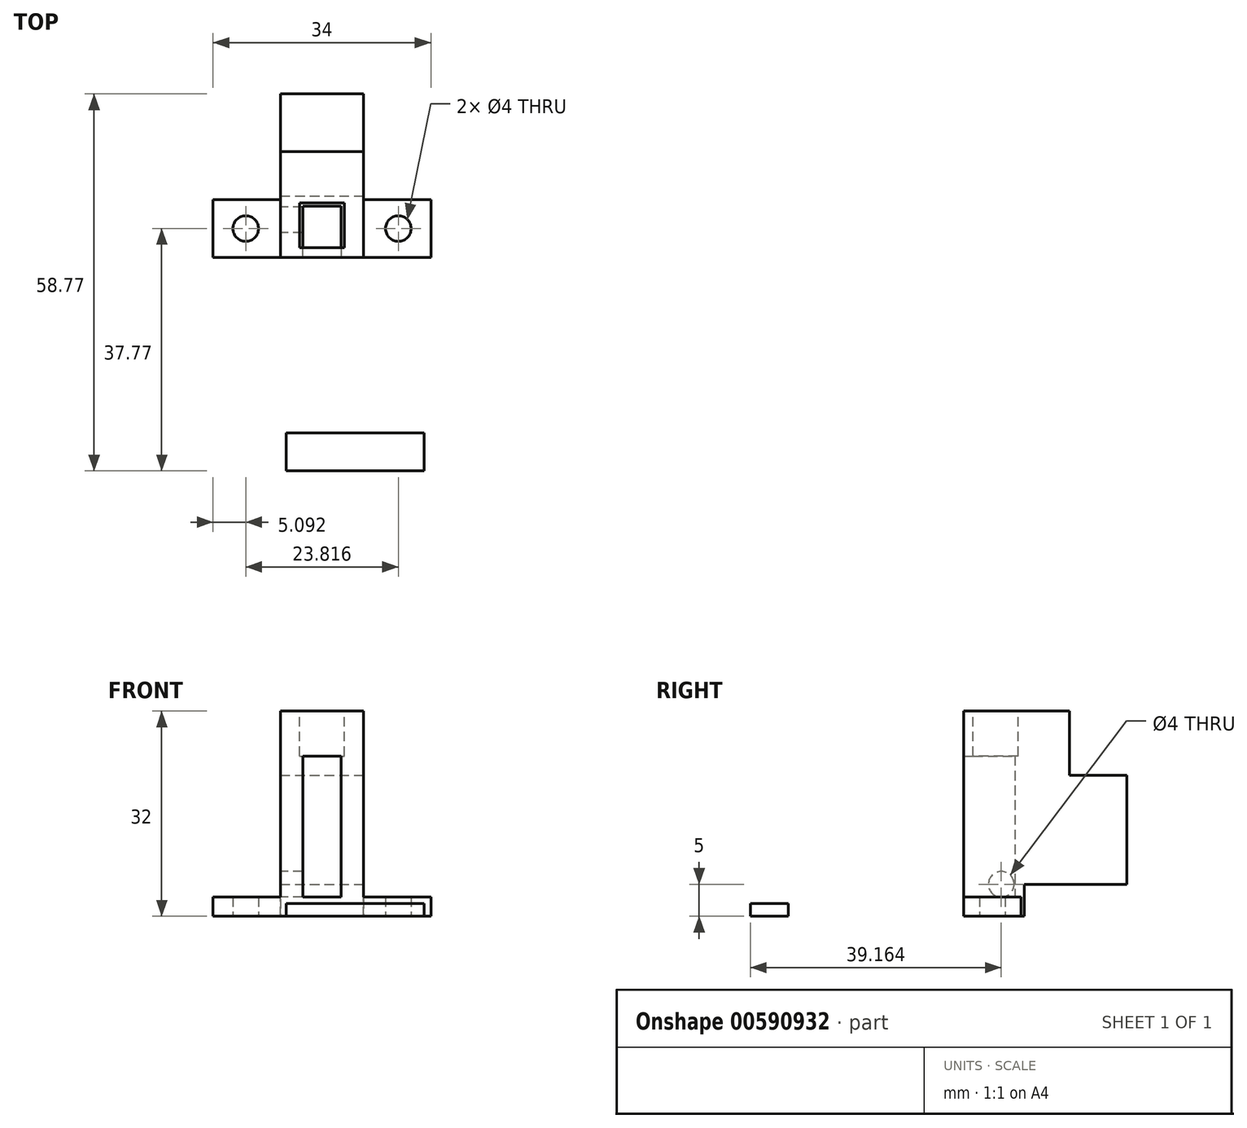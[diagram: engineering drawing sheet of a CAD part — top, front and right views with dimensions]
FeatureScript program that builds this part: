
annotation { "Feature Type Name" : "Feature", "Feature Type Description" : "" }
export const myFeature = defineFeature(function(context is Context, id is Id, definition is map)
    precondition{}
    {
        {
            var Q0;
            Q0=qCreatedBy(makeId("Top.planeOp"),FACE);
            var sketch = newSketch(context, id + "F0", { "sketchPlane" : qUnion([Q0])});
            skLineSegment(sketch, "E0.bottom", {"start": v(-6.5, 20.5) * mm, "end": v(6.5, 20.5) * mm});
            skLineSegment(sketch, "E0.top", {"start": v(-6.5, -5) * mm, "end": v(6.5, -5) * mm});
            skLineSegment(sketch, "E0.left", {"start": v(-6.5, 20.5) * mm, "end": v(-6.5, -5) * mm});
            skLineSegment(sketch, "E0.right", {"start": v(6.5, 20.5) * mm, "end": v(6.5, -5) * mm});
            skSolve(sketch);
        }
        {
            var Q0;
            Q0=makeQuery(id+"F0.imprint","IMPRINT",FACE,{"disambiguationData":[TD([[makeQuery(id+"F0.imprint","IMPRINT",EDGE,{"derivedFrom":sQuery(id+"F0.wireOp",EDGE,"E0.bottom")}),-1.0]])]});
            var Q1;
            Q1=makeQuery(id+"F0.imprint","IMPRINT",FACE,{"disambiguationData":[TD([[makeQuery(id+"F0.imprint","IMPRINT",EDGE,{"derivedFrom":sQuery(id+"F0.wireOp",EDGE,"DMgWt05r-v9AS-qHSY-Eq6J-6PHM9xyc8q6q.bottom")}),-1.0]])]});
            extrude(context, id + "F1", {"entities" : qUnion([Q0, Q1]), "depth" : 32 * mm, "offsetDistance" : 25 * mm});
        }
        {
            var Q0;
            Q0=makeQuery(id+"F1.opExtrude","CAP_FACE",FACE,{"disambiguationData":[OSD([sQuery(id+"F0.wireOp",EDGE,"E0.bottom"),sQuery(id+"F0.wireOp",EDGE,"E0.top"),sQuery(id+"F0.wireOp",EDGE,"E0.left"),sQuery(id+"F0.wireOp",EDGE,"E0.right")])],"isStart":false});
            var sketch = newSketch(context, id + "F2", { "sketchPlane" : qUnion([Q0])});
            skLineSegment(sketch, "E1.bottom", {"start": v(-3.5, 3.5) * mm, "end": v(3.5, 3.5) * mm});
            skLineSegment(sketch, "E1.top", {"start": v(-3.5, -3.5) * mm, "end": v(3.5, -3.5) * mm});
            skLineSegment(sketch, "E1.left", {"start": v(-3.5, 3.5) * mm, "end": v(-3.5, -3.5) * mm});
            skLineSegment(sketch, "E1.right", {"start": v(3.5, 3.5) * mm, "end": v(3.5, -3.5) * mm});
            skPoint(sketch, "E1.middle", {"position": v(0, 0) * mm});
            skLineSegment(sketch, "E2.bottom", {"start": v(6.5, 20.5) * mm, "end": v(-6.5, 20.5) * mm});
            skLineSegment(sketch, "E2.top", {"start": v(6.5, 11.5) * mm, "end": v(-6.5, 11.5) * mm});
            skLineSegment(sketch, "E2.left", {"start": v(6.5, 20.5) * mm, "end": v(6.5, 11.5) * mm});
            skLineSegment(sketch, "E2.right", {"start": v(-6.5, 20.5) * mm, "end": v(-6.5, 11.5) * mm});
            skSolve(sketch);
        }
        {
            var Q0;
            Q0=makeQuery(id+"F2.imprint","IMPRINT",FACE,{"disambiguationData":[TD([[makeQuery(id+"F2.imprint","IMPRINT",EDGE,{"derivedFrom":sQuery(id+"F2.wireOp",EDGE,"E1.bottom")}),-1.0]])]});
            extrude(context, id + "F3", {"entities" : qUnion([Q0]), "operationType" : NewBodyOperationType.REMOVE, "oppositeDirection" : true, "depth" : 7 * mm, "offsetDistance" : 25 * mm});
        }
        {
            var Q0;
            Q0=makeQuery(id+"F0.imprint","IMPRINT",FACE,{"disambiguationData":[TD([[makeQuery(id+"F0.imprint","IMPRINT",EDGE,{"derivedFrom":sQuery(id+"F0.wireOp",EDGE,"E0.bottom")}),-1.0]])]});
            var sketch = newSketch(context, id + "F4", { "sketchPlane" : qUnion([Q0])});
            skLineSegment(sketch, "E3.top", {"start": v(-3, 3) * mm, "end": v(3, 3) * mm});
            skLineSegment(sketch, "E3.left", {"start": v(-3, -3) * mm, "end": v(-3, 3) * mm});
            skLineSegment(sketch, "E3.right", {"start": v(3, -3) * mm, "end": v(3, 3) * mm});
            skPoint(sketch, "E3.middle", {"position": v(0, 0) * mm});
            skLineSegment(sketch, "E4.top", {"start": v(-3, -7.38) * mm, "end": v(3, -7.38) * mm});
            skLineSegment(sketch, "E4.left", {"start": v(-3, -3) * mm, "end": v(-3, -7.38) * mm});
            skLineSegment(sketch, "E4.right", {"start": v(3, -3) * mm, "end": v(3, -7.38) * mm});
            skSolve(sketch);
        }
        {
            var Q0;
            Q0=makeQuery(id+"F4.imprint","IMPRINT",FACE,{"disambiguationData":[TD([[makeQuery(id+"F4.imprint","IMPRINT",EDGE,{"derivedFrom":sQuery(id+"F4.wireOp",EDGE,"E3.top")}),-1.0]])]});
            var Q1;
            {var subQ0=sQuery(id+"F4.wireOp",EDGE,"E4.top");Q1=makeQuery(id+"F4.imprint","IMPRINT",FACE,{"disambiguationData":[TD([[makeQuery(id+"F4.imprint","IMPRINT",EDGE,{"derivedFrom":subQ0}),1.0]])]});}
            extrude(context, id + "F5", {"entities" : qUnion([Q0, Q1]), "operationType" : NewBodyOperationType.REMOVE, "depth" : 25 * mm, "offsetDistance" : 25 * mm});
        }
        {
            var Q0;
            Q0=makeQuery(id+"F2.imprint","IMPRINT",FACE,{"disambiguationData":[TD([[makeQuery(id+"F2.imprint","IMPRINT",EDGE,{"derivedFrom":sQuery(id+"F2.wireOp",EDGE,"E2.bottom")}),-1.0]])]});
            extrude(context, id + "F6", {"entities" : qUnion([Q0]), "operationType" : NewBodyOperationType.REMOVE, "oppositeDirection" : true, "depth" : 10 * mm, "offsetDistance" : 25 * mm});
        }
        {
            var Q0;
            Q0=makeQuery(id+"F0.imprint","IMPRINT",FACE,{"disambiguationData":[TD([[makeQuery(id+"F0.imprint","IMPRINT",EDGE,{"derivedFrom":sQuery(id+"F0.wireOp",EDGE,"E0.bottom")}),-1.0]])]});
            var sketch = newSketch(context, id + "F7", { "sketchPlane" : qUnion([Q0])});
            skLineSegment(sketch, "E5.bottom", {"start": v(-17, -5) * mm, "end": v(17, -5) * mm});
            skLineSegment(sketch, "E5.top", {"start": v(-17, 4) * mm, "end": v(17, 4) * mm});
            skLineSegment(sketch, "E5.left", {"start": v(-17, -5) * mm, "end": v(-17, 4) * mm});
            skLineSegment(sketch, "E5.right", {"start": v(17, -5) * mm, "end": v(17, 4) * mm});
            skLineSegment(sketch, "E6.bottom", {"start": v(7.74, 22.5) * mm, "end": v(-8.26, 22.5) * mm});
            skLineSegment(sketch, "E6.top", {"start": v(7.74, 4.5) * mm, "end": v(-8.26, 4.5) * mm});
            skLineSegment(sketch, "E6.left", {"start": v(7.74, 22.5) * mm, "end": v(7.74, 4.5) * mm});
            skLineSegment(sketch, "E6.right", {"start": v(-8.26, 22.5) * mm, "end": v(-8.26, 4.5) * mm});
            skCircle(sketch, "E7", {"center": v(11.9, -0.5) * mm, "radius": 2 * mm});
            skPoint(sketch, "E7.centerSnap0", {"position": v(17, -0.5) * mm});
            skCircle(sketch, "E8.MirrorC", {"center": v(-11.9, -0.5) * mm, "radius": 2 * mm});
            skSolve(sketch);
        }
        {
            var Q0;
            {var subQ3=sQuery(id+"F7.wireOp",EDGE,"E5.right");Q0=makeQuery(id+"F7.imprint","IMPRINT",FACE,{"disambiguationData":[TD([[makeQuery(id+"F7.imprint","IMPRINT",EDGE,{"derivedFrom":subQ3}),1.0]])]});}
            var Q1;
            {var subQ3=sQuery(id+"F7.wireOp",EDGE,"E5.left");Q1=makeQuery(id+"F7.imprint","IMPRINT",FACE,{"disambiguationData":[TD([[makeQuery(id+"F7.imprint","IMPRINT",EDGE,{"derivedFrom":subQ3}),-1.0]])]});}
            var Q2;
            {var subQ0=sQuery(id+"F7.wireOp",EDGE,"E5.bottom");var subQ1=makeQuery(id+"F0.imprint","IMPRINT",EDGE,{"derivedFrom":sQuery(id+"F0.wireOp",EDGE,"E0.left")});var subQ2=makeQuery(id+"F7.imprint","INTERSECT",VERTEX,{"derivedFrom":[subQ1,subQ0]});Q2=makeQuery(id+"F7.imprint","IMPRINT",FACE,{"disambiguationData":[TD([[makeQuery(id+"F7.imprint","IMPRINT",EDGE,{"disambiguationData":[TD([[subQ2,-1.0]])],"derivedFrom":subQ0}),1.0]])]});}
            extrude(context, id + "F8", {"entities" : qUnion([Q0, Q1, Q2]), "operationType" : NewBodyOperationType.ADD, "depth" : 3 * mm, "offsetDistance" : 25 * mm});
        }
        {
            var Q0;
            Q0=makeQuery(id+"F7.imprint","IMPRINT",FACE,{"disambiguationData":[TD([[makeQuery(id+"F7.imprint","IMPRINT",EDGE,{"derivedFrom":sQuery(id+"F7.wireOp",EDGE,"E6.bottom")}),1.0]])]});
            var Q1;
            {var subQ5=makeQuery(id+"F0.imprint","IMPRINT",EDGE,{"derivedFrom":sQuery(id+"F0.wireOp",EDGE,"E0.bottom")});Q1=makeQuery(id+"F7.imprint","IMPRINT",FACE,{"disambiguationData":[TD([[makeQuery(id+"F7.imprint","IMPRINT",EDGE,{"derivedFrom":subQ5}),-1.0]])]});}
            extrude(context, id + "F9", {"entities" : qUnion([Q0, Q1]), "operationType" : NewBodyOperationType.REMOVE, "depth" : 5 * mm, "offsetDistance" : 25 * mm});
        }
        {
            var Q0;
            Q0=makeQuery(id+"F1.opExtrude","SWEPT_FACE",FACE,{"disambiguationData":[OSD([sQuery(id+"F0.wireOp",EDGE,"E0.left")])]});
            var sketch = newSketch(context, id + "F10", { "sketchPlane" : qUnion([Q0])});
            skCircle(sketch, "E9", {"center": v(-0.9, 5) * mm, "radius": 2 * mm});
            skSolve(sketch);
        }
        {
            var Q0;
            {var subQ0=sQuery(id+"F10.wireOp",EDGE,"E9");var subQ1=sQuery(id+"F7.wireOp",EDGE,"E6.top");var subQ2=makeQuery(id+"F1.opExtrude","SWEPT_FACE",FACE,{"disambiguationData":[OSD([sQuery(id+"F0.wireOp",EDGE,"E0.left")])]});var subQ3=subQ2;var subQ4=makeQuery(id+"F9.boolean.opBoolean","INTERSECT",EDGE,{"derivedFrom":[subQ3,makeQuery(id+"F9.opExtrude","SWEPT_FACE",FACE,{"disambiguationData":[OSD([subQ1])]})]});var subQ5=makeQuery(id+"F10.imprint","INTERSECT",VERTEX,{"derivedFrom":[subQ4,subQ0]});Q0=makeQuery(id+"F10.imprint","IMPRINT",FACE,{"disambiguationData":[TD([[makeQuery(id+"F10.imprint","IMPRINT",EDGE,{"disambiguationData":[TD([[subQ5,-1.0]])],"derivedFrom":subQ0}),1.0]])]});}
            extrude(context, id + "F11", {"entities" : qUnion([Q0]), "operationType" : NewBodyOperationType.REMOVE, "oppositeDirection" : true, "depth" : 7 * mm, "offsetDistance" : 25 * mm});
        }
        {
            var Q0;
            Q0=qCreatedBy(makeId("Top.planeOp"),FACE);
            var sketch = newSketch(context, id + "F12", { "sketchPlane" : qUnion([Q0])});
            skLineSegment(sketch, "E10.bottom", {"start": v(-5.6, -38.27) * mm, "end": v(15.9, -38.27) * mm});
            skLineSegment(sketch, "E10.top", {"start": v(-5.6, -32.37) * mm, "end": v(15.9, -32.37) * mm});
            skLineSegment(sketch, "E10.left", {"start": v(-5.6, -38.27) * mm, "end": v(-5.6, -32.37) * mm});
            skLineSegment(sketch, "E10.right", {"start": v(15.9, -38.27) * mm, "end": v(15.9, -32.37) * mm});
            skSolve(sketch);
        }
        {
            var Q0;
            Q0 = qSketchRegion(id + "F12", true);
            extrude(context, id + "F13", {"entities" : qUnion([Q0]), "depth" : 2 * mm, "offsetDistance" : 25 * mm});
        }
    });
